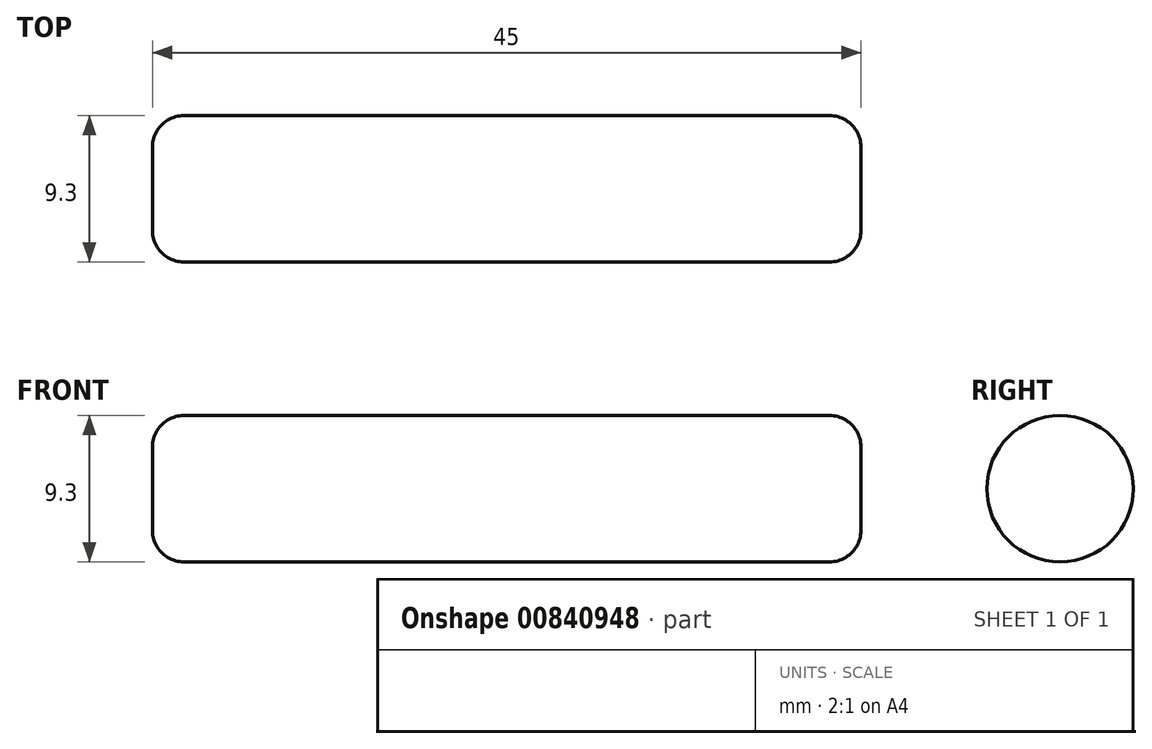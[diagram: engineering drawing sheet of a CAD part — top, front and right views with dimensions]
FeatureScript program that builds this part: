
annotation { "Feature Type Name" : "Feature", "Feature Type Description" : "" }
export const myFeature = defineFeature(function(context is Context, id is Id, definition is map)
    precondition{}
    {
        {
            var Q0;
            Q0=qCreatedBy(makeId("Right.planeOp"),FACE);
            var sketch = newSketch(context, id + "F0", { "sketchPlane" : qUnion([Q0])});
            skCircle(sketch, "E0", {"center": v(0, 0) * mm, "radius": 4.65 * mm});
            skSolve(sketch);
        }
        {
            var Q0;
            Q0 = qSketchRegion(id + "F0", true);
            extrude(context, id + "F1", {"entities" : qUnion([Q0]), "depth" : 45 * mm, "offsetDistance" : 25 * mm});
        }
        {
            var Q0;
            Q0=makeQuery(id+"F1.opExtrude","CAP_EDGE",EDGE,{"disambiguationData":[OSD([sQuery(id+"F0.wireOp",EDGE,"E0")])],"isStart":true});
            fillet(context, id + "F2", {"entities" : qUnion([Q0]), "radius" : 2 * mm, "tangentPropagation" : true, "allowEdgeOverflow" : false});
        }
        {
            var Q0;
            Q0=makeQuery(id+"F1.opExtrude","CAP_EDGE",EDGE,{"disambiguationData":[OSD([sQuery(id+"F0.wireOp",EDGE,"E0")])],"isStart":false});
            fillet(context, id + "F3", {"entities" : qUnion([Q0]), "radius" : 2 * mm, "tangentPropagation" : true, "allowEdgeOverflow" : false});
        }
    });
